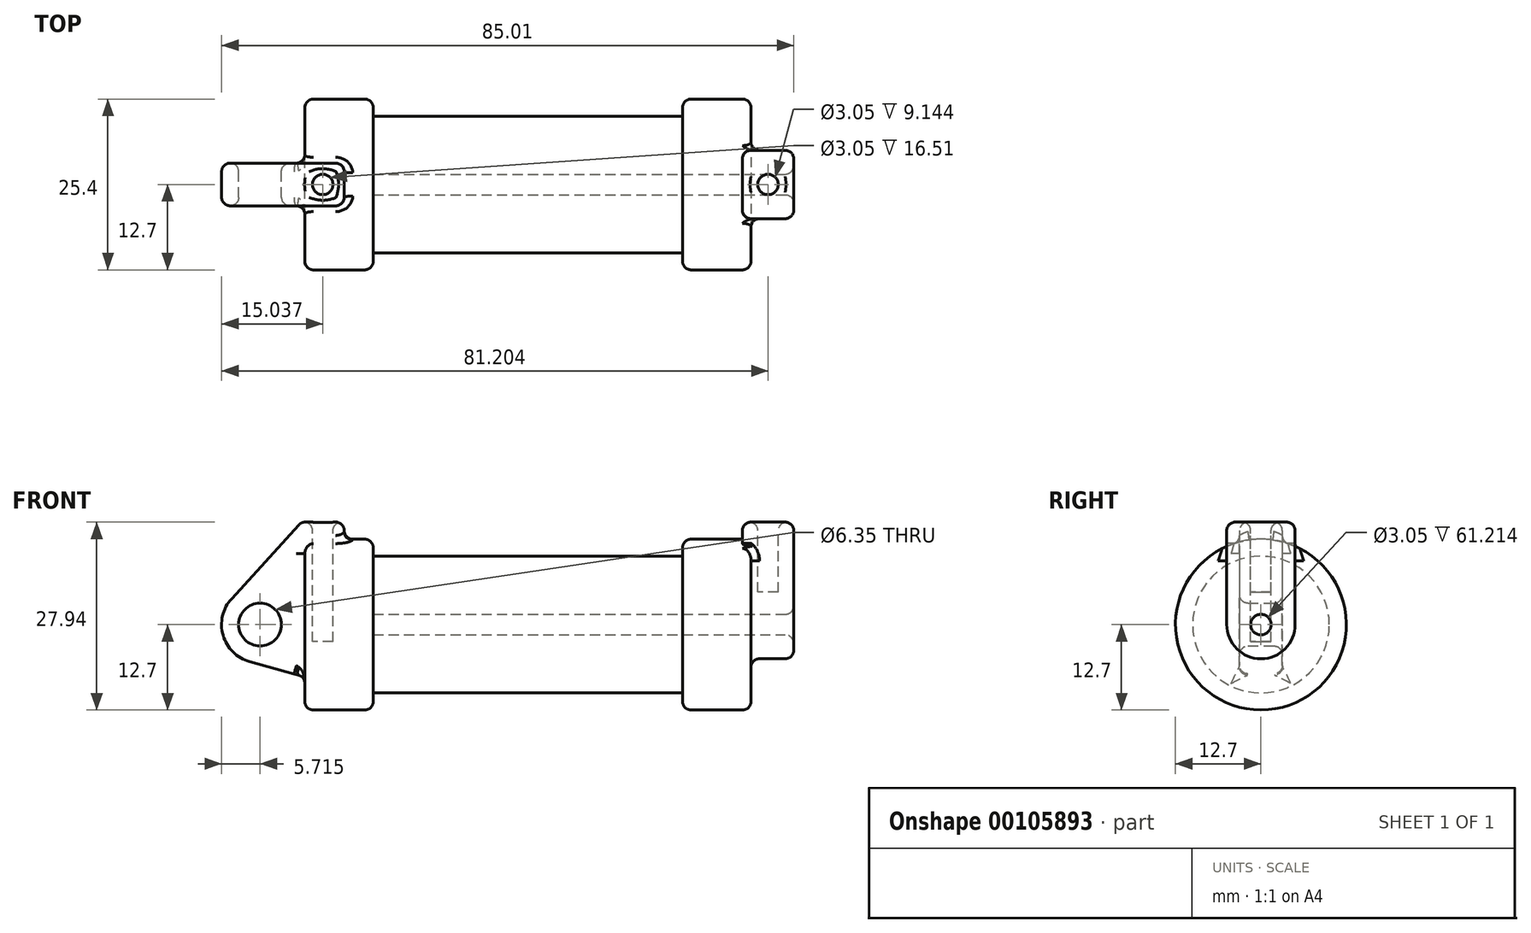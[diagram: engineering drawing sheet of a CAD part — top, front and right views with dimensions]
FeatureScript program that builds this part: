
annotation { "Feature Type Name" : "Feature", "Feature Type Description" : "" }
export const myFeature = defineFeature(function(context is Context, id is Id, definition is map)
    precondition{}
    {
        {
            var Q0;
            Q0=qCreatedBy(makeId("Front.planeOp"),FACE);
            var sketch = newSketch(context, id + "F0", { "sketchPlane" : qUnion([Q0])});
            skLineSegment(sketch, "E0", {"start": v(0, 0) * mm, "end": v(0, 12.7) * mm});
            skLineSegment(sketch, "E1", {"start": v(0, 12.7) * mm, "end": v(10.16, 12.7) * mm});
            skLineSegment(sketch, "E2", {"start": v(10.16, 12.7) * mm, "end": v(10.16, 10.16) * mm});
            skLineSegment(sketch, "E3", {"start": v(10.16, 10.16) * mm, "end": v(56.13, 10.16) * mm});
            skLineSegment(sketch, "E4", {"start": v(56.13, 10.16) * mm, "end": v(56.13, 12.7) * mm});
            skLineSegment(sketch, "E5", {"start": v(56.13, 12.7) * mm, "end": v(66.3, 12.7) * mm});
            skLineSegment(sketch, "E6", {"start": v(66.3, 12.7) * mm, "end": v(66.3, 0) * mm});
            skLineSegment(sketch, "E7", {"start": v(66.3, 0) * mm, "end": v(0, 0) * mm});
            skLineSegment(sketch, "E8", {"start": v(5.84, 15.24) * mm, "end": v(-0.5, 15.24) * mm});
            skLineSegment(sketch, "E9", {"start": v(-0.5, 15.24) * mm, "end": v(-10.88, 3.85) * mm});
            skLineSegment(sketch, "E10", {"start": v(0, 0) * mm, "end": v(-6.65, 0) * mm});
            skCircle(sketch, "E11", {"center": v(-6.65, 0) * mm, "radius": 5.72 * mm});
            skCircle(sketch, "E12", {"center": v(-6.65, 0) * mm, "radius": 3.18 * mm});
            skLineSegment(sketch, "E13", {"start": v(5.84, 15.24) * mm, "end": v(5.84, -9.4) * mm});
            skLineSegment(sketch, "E14", {"start": v(5.84, -9.4) * mm, "end": v(-8.18, -5.5) * mm});
            skSolve(sketch);
        }
        {
            var Q0;
            {var subQ0=sQuery(id+"F0.wireOp",EDGE,"E0");Q0=makeQuery(id+"F0.imprint","IMPRINT",FACE,{"disambiguationData":[TD([[makeQuery(id+"F0.imprint","IMPRINT",EDGE,{"derivedFrom":subQ0}),-1.0]])]});}
            var Q1;
            {var subQ0=sQuery(id+"F0.wireOp",EDGE,"E2");Q1=makeQuery(id+"F0.imprint","IMPRINT",FACE,{"disambiguationData":[TD([[makeQuery(id+"F0.imprint","IMPRINT",EDGE,{"derivedFrom":subQ0}),-1.0]])]});}
            var Q2;
            Q2=sQuery(id+"F0.wireOp",EDGE,"E7");
            revolve(context, id + "F1", {"entities" : qUnion([Q0, Q1]), "axis" : qUnion([Q2]), "revolveType" : RevolveType.FULL});
        }
        {
            var Q0;
            {var subQ3=sQuery(id+"F0.wireOp",EDGE,"E0");Q0=makeQuery(id+"F0.imprint","IMPRINT",FACE,{"disambiguationData":[TD([[makeQuery(id+"F0.imprint","IMPRINT",EDGE,{"derivedFrom":subQ3}),1.0]])]});}
            var Q1;
            {var subQ0=sQuery(id+"F0.wireOp",EDGE,"E14");Q1=makeQuery(id+"F0.imprint","IMPRINT",FACE,{"disambiguationData":[TD([[makeQuery(id+"F0.imprint","IMPRINT",EDGE,{"derivedFrom":subQ0}),-1.0]])]});}
            var Q2;
            {var subQ4=sQuery(id+"F0.wireOp",EDGE,"E12");Q2=makeQuery(id+"F0.imprint","IMPRINT",FACE,{"disambiguationData":[TD([[makeQuery(id+"F0.imprint","IMPRINT",EDGE,{"derivedFrom":subQ4}),-1.0]])]});}
            var Q3;
            {var subQ0=sQuery(id+"F0.wireOp",EDGE,"E0");Q3=makeQuery(id+"F0.imprint","IMPRINT",FACE,{"disambiguationData":[TD([[makeQuery(id+"F0.imprint","IMPRINT",EDGE,{"derivedFrom":subQ0}),-1.0]])]});}
            extrude(context, id + "F2", {"entities" : qUnion([Q0, Q1, Q2, Q3]), "operationType" : NewBodyOperationType.ADD, "endBound" : BoundingType.SYMMETRIC, "depth" : 6.35 * mm});
        }
        {
            var Q0;
            Q0=makeQuery(id+"F1.opRevolve","SWEPT_FACE",FACE,{"disambiguationData":[OSD([sQuery(id+"F0.wireOp",EDGE,"E6")])]});
            var sketch = newSketch(context, id + "F3", { "sketchPlane" : qUnion([Q0])});
            skCircle(sketch, "E15", {"center": v(0, 0) * mm, "radius": 5.08 * mm});
            skCircle(sketch, "E16", {"center": v(0, 0) * mm, "radius": 1.52 * mm});
            skLineSegment(sketch, "E17", {"start": v(-5.08, 0) * mm, "end": v(-5.08, 15.24) * mm});
            skLineSegment(sketch, "E18", {"start": v(5.08, 0) * mm, "end": v(5.08, 15.24) * mm});
            skLineSegment(sketch, "E19", {"start": v(-5.08, 15.24) * mm, "end": v(5.08, 15.24) * mm});
            skSolve(sketch);
        }
        {
            var Q0;
            {var subQ0=sQuery(id+"F3.wireOp",EDGE,"E17");var subQ1=sQuery(id+"F3.wireOp",EDGE,"E15");var subQ2=makeQuery(id+"F3.imprint","INTERSECT",VERTEX,{"derivedFrom":[subQ1,subQ0]});Q0=makeQuery(id+"F3.imprint","IMPRINT",FACE,{"disambiguationData":[TD([[makeQuery(id+"F3.imprint","IMPRINT",EDGE,{"disambiguationData":[TD([[subQ2,1.0]])],"derivedFrom":subQ1}),-1.0]])]});}
            var Q1;
            {var subQ0=sQuery(id+"F3.wireOp",EDGE,"E19");Q1=makeQuery(id+"F3.imprint","IMPRINT",FACE,{"disambiguationData":[TD([[makeQuery(id+"F3.imprint","IMPRINT",EDGE,{"derivedFrom":subQ0}),-1.0]])]});}
            var Q2;
            Q2=makeQuery(id+"F3.imprint","IMPRINT",FACE,{"disambiguationData":[TD([[makeQuery(id+"F3.imprint","IMPRINT",EDGE,{"derivedFrom":sQuery(id+"F3.wireOp",EDGE,"E16")}),-1.0]])]});
            extrude(context, id + "F4", {"entities" : qUnion([Q0, Q1, Q2]), "oppositeDirection" : true, "depth" : 1.27 * mm});
        }
        {
            var Q0;
            Q0=makeQuery(id+"F4.opExtrude","CAP_FACE",FACE,{"disambiguationData":[OSD([sQuery(id+"F3.wireOp",EDGE,"E15"),sQuery(id+"F3.wireOp",EDGE,"E16"),sQuery(id+"F3.wireOp",EDGE,"E17"),sQuery(id+"F3.wireOp",EDGE,"E18"),sQuery(id+"F3.wireOp",EDGE,"E19")])],"isStart":true});
            extrude(context, id + "F5", {"entities" : qUnion([Q0]), "operationType" : NewBodyOperationType.ADD, "depth" : 6.35 * mm});
        }
        {
            var Q0;
            {var subQ0=sQuery(id+"F3.wireOp",EDGE,"E16");Q0=makeQuery(id+"F5.boolean.opBoolean","SPLIT",FACE,{"disambiguationData":[TD([makeQuery(id+"F4.opExtrude","SWEPT_FACE",FACE,{"disambiguationData":[OSD([subQ0])]})])],"derivedFrom":makeQuery(id+"F1.opRevolve","SWEPT_FACE",FACE,{"disambiguationData":[OSD([sQuery(id+"F0.wireOp",EDGE,"E6")])]})});}
            var Q1;
            Q1=makeQuery(id+"F1.opRevolve","SWEPT_FACE",FACE,{"disambiguationData":[OSD([sQuery(id+"F0.wireOp",EDGE,"E2")])]});
            extrude(context, id + "F6", {"entities" : qUnion([Q0]), "operationType" : NewBodyOperationType.REMOVE, "endBound" : BoundingType.UP_TO_SURFACE, "oppositeDirection" : true, "endBoundEntityFace" : qUnion([Q1]), "depth" : 25.4 * mm});
        }
        {
            var Q0;
            Q0=makeQuery(id+"F2.opExtrude","SWEPT_FACE",FACE,{"disambiguationData":[OSD([sQuery(id+"F0.wireOp",EDGE,"E8")])]});
            var sketch = newSketch(context, id + "F7", { "sketchPlane" : qUnion([Q0])});
            skCircle(sketch, "E20", {"center": v(2.67, 0) * mm, "radius": 1.52 * mm});
            skSolve(sketch);
        }
        {
            var Q0;
            {var subQ0=sQuery(id+"F3.wireOp",EDGE,"E19");Q0=makeQuery(id+"F5.boolean.opBoolean","MERGE",FACE,{"derivedFrom":[makeQuery(id+"F4.opExtrude","SWEPT_FACE",FACE,{"disambiguationData":[OSD([subQ0])]}),makeQuery(id+"F5.opExtrude","SWEPT_FACE",FACE,{"disambiguationData":[OSD([subQ0])]})]});}
            var sketch = newSketch(context, id + "F8", { "sketchPlane" : qUnion([Q0])});
            skLineSegment(sketch, "E21", {"start": v(65.02, 0) * mm, "end": v(72.64, 0) * mm, "construction": true});
            skLineSegment(sketch, "E22", {"start": v(68.83, 5.08) * mm, "end": v(68.83, -5.08) * mm, "construction": true});
            skCircle(sketch, "E23", {"center": v(68.83, 0) * mm, "radius": 1.52 * mm});
            skSolve(sketch);
        }
        {
            var Q0;
            Q0=makeQuery(id+"F8.imprint","IMPRINT",FACE,{"disambiguationData":[TD([[makeQuery(id+"F8.imprint","IMPRINT",EDGE,{"derivedFrom":sQuery(id+"F8.wireOp",EDGE,"E23")}),1.0]])]});
            extrude(context, id + "F9", {"entities" : qUnion([Q0]), "operationType" : NewBodyOperationType.REMOVE, "oppositeDirection" : true, "depth" : 10.4 * mm});
        }
        {
            var Q0;
            Q0=makeQuery(id+"F7.imprint","IMPRINT",FACE,{"disambiguationData":[TD([[makeQuery(id+"F7.imprint","IMPRINT",EDGE,{"derivedFrom":sQuery(id+"F7.wireOp",EDGE,"E20")}),1.0]])]});
            extrude(context, id + "F10", {"entities" : qUnion([Q0]), "operationType" : NewBodyOperationType.REMOVE, "oppositeDirection" : true, "depth" : 17.78 * mm});
        }
        {
            var Q0;
            Q0=makeQuery(id+"F1.opRevolve","SWEPT_EDGE",EDGE,{"disambiguationData":[OSD([sQuery(id+"F0.wireOp",EDGE,"E1"),sQuery(id+"F0.wireOp",EDGE,"E2")])]});
            var Q1;
            Q1=makeQuery(id+"F1.opRevolve","SWEPT_EDGE",EDGE,{"disambiguationData":[OSD([sQuery(id+"F0.wireOp",EDGE,"E4"),sQuery(id+"F0.wireOp",EDGE,"E5")])]});
            var Q2;
            Q2=makeQuery(id+"F1.opRevolve","SWEPT_FACE",FACE,{"disambiguationData":[OSD([sQuery(id+"F0.wireOp",EDGE,"E0")])]});
            var Q3;
            Q3=makeQuery(id+"F5.boolean.opBoolean","SPLIT",FACE,{"disambiguationData":[TD([makeQuery(id+"F1.opRevolve","SWEPT_FACE",FACE,{"disambiguationData":[OSD([sQuery(id+"F0.wireOp",EDGE,"E5")])]})])],"derivedFrom":makeQuery(id+"F1.opRevolve","SWEPT_FACE",FACE,{"disambiguationData":[OSD([sQuery(id+"F0.wireOp",EDGE,"E6")])]})});
            fillet(context, id + "F11", {"entities" : qUnion([Q0, Q1, Q2, Q3]), "radius" : 1.27 * mm, "tangentPropagation" : true, "allowEdgeOverflow" : false});
        }
        {
            var Q0;
            {var subQ0=sQuery(id+"F3.wireOp",EDGE,"E18");Q0=makeQuery(id+"F5.boolean.opBoolean","MERGE",FACE,{"derivedFrom":[makeQuery(id+"F4.opExtrude","SWEPT_FACE",FACE,{"disambiguationData":[OSD([subQ0])]}),makeQuery(id+"F5.opExtrude","SWEPT_FACE",FACE,{"disambiguationData":[OSD([subQ0])]})]});}
            var Q1;
            Q1=makeQuery(id+"F5.opExtrude","CAP_FACE",FACE,{"disambiguationData":[OSD([sQuery(id+"F3.wireOp",EDGE,"E15"),sQuery(id+"F3.wireOp",EDGE,"E16"),sQuery(id+"F3.wireOp",EDGE,"E17"),sQuery(id+"F3.wireOp",EDGE,"E18"),sQuery(id+"F3.wireOp",EDGE,"E19")])],"isStart":false});
            var Q2;
            Q2=makeQuery(id+"F5.opExtrude","CAP_EDGE",EDGE,{"disambiguationData":[OSD([sQuery(id+"F3.wireOp",EDGE,"E19")])],"isStart":false});
            var Q3;
            {var subQ0=sQuery(id+"F3.wireOp",EDGE,"E19");Q3=makeQuery(id+"F5.boolean.opBoolean","MERGE",FACE,{"derivedFrom":[makeQuery(id+"F4.opExtrude","SWEPT_FACE",FACE,{"disambiguationData":[OSD([subQ0])]}),makeQuery(id+"F5.opExtrude","SWEPT_FACE",FACE,{"disambiguationData":[OSD([subQ0])]})]});}
            var Q4;
            {var subQ0=sQuery(id+"F3.wireOp",EDGE,"E15");Q4=makeQuery(id+"F5.boolean.opBoolean","MERGE",FACE,{"derivedFrom":[makeQuery(id+"F4.opExtrude","SWEPT_FACE",FACE,{"disambiguationData":[OSD([subQ0])]}),makeQuery(id+"F5.opExtrude","SWEPT_FACE",FACE,{"disambiguationData":[OSD([subQ0])]})]});}
            var Q5;
            {var subQ0=sQuery(id+"F3.wireOp",EDGE,"E17");Q5=makeQuery(id+"F5.boolean.opBoolean","MERGE",FACE,{"derivedFrom":[makeQuery(id+"F4.opExtrude","SWEPT_FACE",FACE,{"disambiguationData":[OSD([subQ0])]}),makeQuery(id+"F5.opExtrude","SWEPT_FACE",FACE,{"disambiguationData":[OSD([subQ0])]})]});}
            fillet(context, id + "F12", {"entities" : qUnion([Q0, Q1, Q2, Q3, Q4, Q5]), "radius" : 1.27 * mm, "tangentPropagation" : true, "allowEdgeOverflow" : false});
        }
        {
            var Q0;
            Q0=makeQuery(id+"F2.opExtrude","CAP_FACE",FACE,{"disambiguationData":[OSD([sQuery(id+"F0.wireOp",EDGE,"E8"),sQuery(id+"F0.wireOp",EDGE,"E9"),sQuery(id+"F0.wireOp",EDGE,"E11"),sQuery(id+"F0.wireOp",EDGE,"E12"),sQuery(id+"F0.wireOp",EDGE,"E13"),sQuery(id+"F0.wireOp",EDGE,"E14")])],"isStart":false});
            var Q1;
            Q1=makeQuery(id+"F2.opExtrude","SWEPT_FACE",FACE,{"disambiguationData":[OSD([sQuery(id+"F0.wireOp",EDGE,"E8")])]});
            var Q2;
            Q2=makeQuery(id+"F2.opExtrude","SWEPT_FACE",FACE,{"disambiguationData":[OSD([sQuery(id+"F0.wireOp",EDGE,"E13")])]});
            var Q3;
            Q3=makeQuery(id+"F2.opExtrude","SWEPT_FACE",FACE,{"disambiguationData":[OSD([sQuery(id+"F0.wireOp",EDGE,"E9")])]});
            var Q4;
            Q4=makeQuery(id+"F2.opExtrude","SWEPT_FACE",FACE,{"disambiguationData":[OSD([sQuery(id+"F0.wireOp",EDGE,"E11")])]});
            var Q5;
            Q5=makeQuery(id+"F2.opExtrude","SWEPT_FACE",FACE,{"disambiguationData":[OSD([sQuery(id+"F0.wireOp",EDGE,"E14")])]});
            var Q6;
            Q6=makeQuery(id+"F2.opExtrude","CAP_FACE",FACE,{"disambiguationData":[OSD([sQuery(id+"F0.wireOp",EDGE,"E8"),sQuery(id+"F0.wireOp",EDGE,"E9"),sQuery(id+"F0.wireOp",EDGE,"E11"),sQuery(id+"F0.wireOp",EDGE,"E12"),sQuery(id+"F0.wireOp",EDGE,"E13"),sQuery(id+"F0.wireOp",EDGE,"E14")])],"isStart":true});
            fillet(context, id + "F13", {"entities" : qUnion([Q0, Q1, Q2, Q3, Q4, Q5, Q6]), "radius" : 1.27 * mm, "tangentPropagation" : true, "allowEdgeOverflow" : false});
        }
    });
